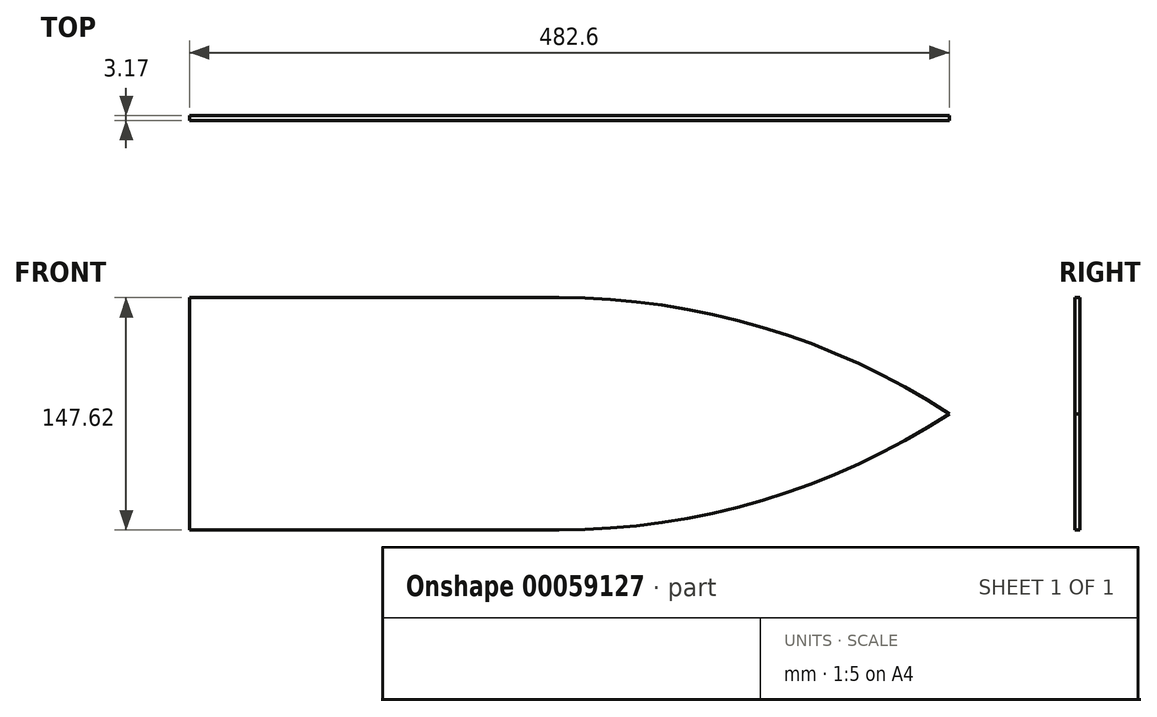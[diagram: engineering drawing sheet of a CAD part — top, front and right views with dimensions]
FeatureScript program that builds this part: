
annotation { "Feature Type Name" : "Feature", "Feature Type Description" : "" }
export const myFeature = defineFeature(function(context is Context, id is Id, definition is map)
    precondition{}
    {
        {
            var Q0;
            Q0=qCreatedBy(makeId("Front.planeOp"),FACE);
            var sketch = newSketch(context, id + "F0", { "sketchPlane" : qUnion([Q0])});
            skLineSegment(sketch, "E0", {"start": v(-232.12, 39.13) * mm, "end": v(250.48, 39.13) * mm});
            skLineSegment(sketch, "E1", {"start": v(-232.12, 39.13) * mm, "end": v(-232.12, 112.94) * mm});
            skLineSegment(sketch, "E2", {"start": v(-232.12, 112.94) * mm, "end": v(2.56, 112.94) * mm});
            skArc(sketch, "E3", {"start": v(250.48, 39.13) * mm, "mid": v(131.9, 94.1) * mm, "end": v(2.56, 112.94) * mm});
            skSolve(sketch);
        }
        {
            var Q0;
            Q0=qSketchRegion(id+"F0",true);
            extrude(context, id + "F1", {"entities" : qUnion([Q0]), "depth" : 3.17 * mm});
        }
        {
            var Q0;
            Q0=makeQuery(id+"F1.opExtrude","SWEPT_BODY",BODY,{"disambiguationData":[OSD([sQuery(id+"F0.wireOp",EDGE,"E0"),sQuery(id+"F0.wireOp",EDGE,"E1"),sQuery(id+"F0.wireOp",EDGE,"E2"),sQuery(id+"F0.wireOp",EDGE,"E3")])]});
            var Q1;
            Q1=makeQuery(id+"F1.opExtrude","SWEPT_FACE",FACE,{"disambiguationData":[OSD([sQuery(id+"F0.wireOp",EDGE,"E0")])]});
            mirror(context, id + "F2", {"operationType" : NewBodyOperationType.ADD, "entities" : qUnion([Q0]), "mirrorPlane" : qUnion([Q1])});
        }
    });
